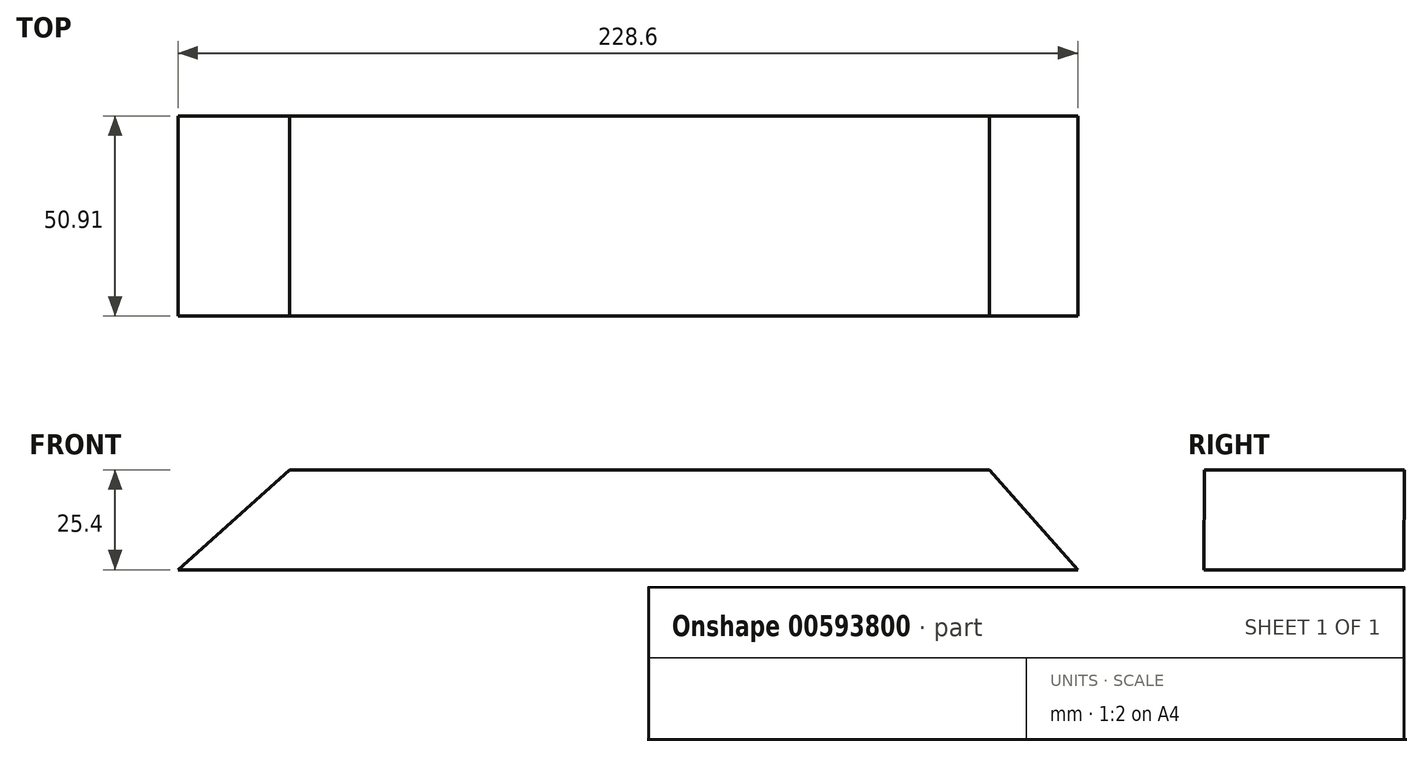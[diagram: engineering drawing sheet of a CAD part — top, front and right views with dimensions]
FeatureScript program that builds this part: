
annotation { "Feature Type Name" : "Feature", "Feature Type Description" : "" }
export const myFeature = defineFeature(function(context is Context, id is Id, definition is map)
    precondition{}
    {
        {
            var Q0;
            Q0=qCreatedBy(makeId("Top.planeOp"),FACE);
            var sketch = newSketch(context, id + "F0", { "sketchPlane" : qUnion([Q0])});
            skLineSegment(sketch, "E0.bottom", {"start": v(-98.79, -3.18) * mm, "end": v(129.81, -3.18) * mm});
            skLineSegment(sketch, "E0.top", {"start": v(-98.79, -53.98) * mm, "end": v(129.81, -53.98) * mm});
            skLineSegment(sketch, "E0.left", {"start": v(-98.79, -3.18) * mm, "end": v(-98.79, -53.98) * mm});
            skLineSegment(sketch, "E0.right", {"start": v(129.81, -3.18) * mm, "end": v(129.81, -53.98) * mm});
            skSolve(sketch);
        }
        {
            var Q0;
            Q0=makeQuery(id+"F0.imprint","IMPRINT",FACE,{"disambiguationData":[TD([[makeQuery(id+"F0.imprint","IMPRINT",EDGE,{"derivedFrom":sQuery(id+"F0.wireOp",EDGE,"E0.bottom")}),-1.0]])]});
            cPlane(context, id + "F1", {"entities" : qUnion([Q0]), "cplaneType" : CPlaneType.OFFSET, "offset" : 25.4 * mm, "width" : 152.4 * mm, "height" : 152.4 * mm});
        }
        {
            var Q0;
            Q0=qCreatedBy(id+"F1.planeOp",FACE);
            var sketch = newSketch(context, id + "F2", { "sketchPlane" : qUnion([Q0])});
            skLineSegment(sketch, "E1.bottom", {"start": v(-70.42, -3.07) * mm, "end": v(107.38, -3.07) * mm});
            skLineSegment(sketch, "E1.top", {"start": v(-70.42, -53.87) * mm, "end": v(107.38, -53.87) * mm});
            skLineSegment(sketch, "E1.left", {"start": v(-70.42, -3.07) * mm, "end": v(-70.42, -53.87) * mm});
            skLineSegment(sketch, "E1.right", {"start": v(107.38, -3.07) * mm, "end": v(107.38, -53.87) * mm});
            skSolve(sketch);
        }
        {
            var Q0;
            Q0=makeQuery(id+"F2.imprint","IMPRINT",FACE,{"disambiguationData":[TD([[makeQuery(id+"F2.imprint","IMPRINT",EDGE,{"derivedFrom":sQuery(id+"F2.wireOp",EDGE,"E1.bottom")}),-1.0]])]});
            var Q1;
            Q1=makeQuery(id+"F0.imprint","IMPRINT",FACE,{"disambiguationData":[TD([[makeQuery(id+"F0.imprint","IMPRINT",EDGE,{"derivedFrom":sQuery(id+"F0.wireOp",EDGE,"E0.bottom")}),-1.0]])]});
            loft(context, id + "F3", {"sheetProfilesArray" : [{ "sheetProfileEntities" : qUnion([Q0]) }, { "sheetProfileEntities" : qUnion([Q1]) }]});
        }
        {
            var Q0;
            Q0=qCreatedBy(makeId("Front.planeOp"),FACE);
            var sketch = newSketch(context, id + "F4", { "sketchPlane" : qUnion([Q0])});
            skLineSegment(sketch, "E2", {"start": v(106.78, 25.44) * mm, "end": v(78.3, 0) * mm});
            skLineSegment(sketch, "E3", {"start": v(78.3, 0) * mm, "end": v(49.32, 24.85) * mm});
            skLineSegment(sketch, "E4", {"start": v(49.32, 24.85) * mm, "end": v(20.34, 0) * mm});
            skLineSegment(sketch, "E5", {"start": v(20.34, 0) * mm, "end": v(-8.39, 24.85) * mm});
            skLineSegment(sketch, "E6", {"start": v(-8.39, 24.85) * mm, "end": v(-36.72, 0) * mm});
            skLineSegment(sketch, "E7", {"start": v(-36.72, 0) * mm, "end": v(-69.9, 24.85) * mm});
            skSolve(sketch);
        }
        {
            var Q0;
            Q0 = qSketchRegion(id + "F4", true);
            var Q1;
            Q1 = qConstructionFilter(qBodyType(qCreatedBy(id + "F4" ,EDGE), BodyType.WIRE), ConstructionObject.NO);
            extrude(context, id + "F5", {"entities" : qUnion([Q0]), "bodyType" : ToolBodyType.SURFACE, "surfaceEntities" : qUnion([Q1]), "depth" : 55.12 * mm, "offsetDistance" : 25.4 * mm});
        }
    });
